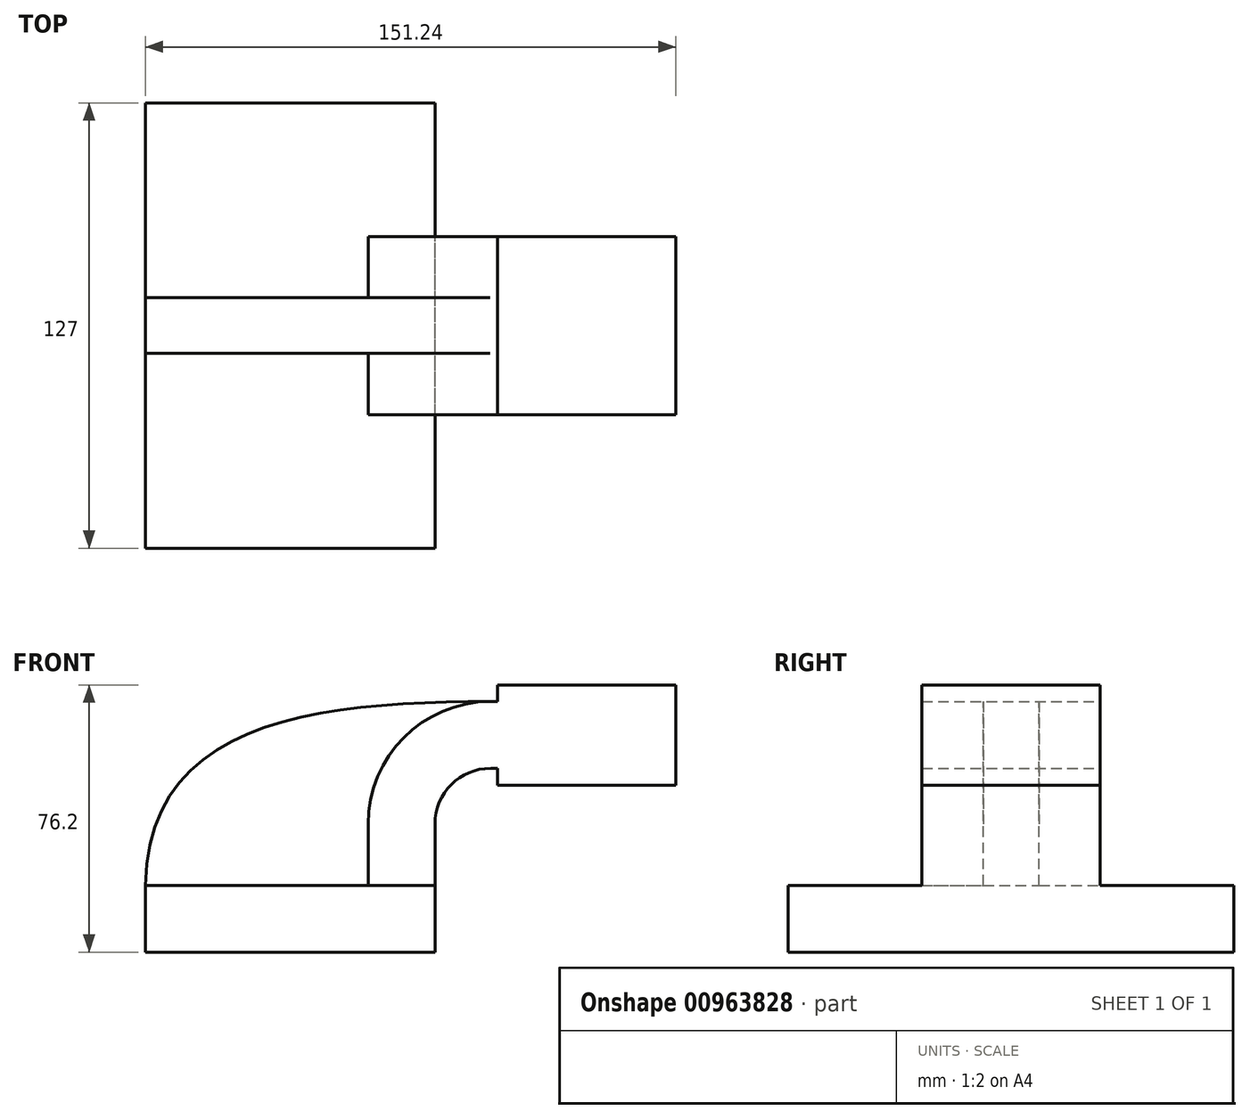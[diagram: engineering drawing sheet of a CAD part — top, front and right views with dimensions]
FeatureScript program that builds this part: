
annotation { "Feature Type Name" : "Feature", "Feature Type Description" : "" }
export const myFeature = defineFeature(function(context is Context, id is Id, definition is map)
    precondition{}
    {
        {
            var Q0;
            Q0=qCreatedBy(makeId("Front.planeOp"),FACE);
            var sketch = newSketch(context, id + "F0", { "sketchPlane" : qUnion([Q0])});
            skLineSegment(sketch, "E0.bottom", {"start": v(-41.28, -9.53) * mm, "end": v(41.28, -9.53) * mm});
            skLineSegment(sketch, "E0.top", {"start": v(-41.28, 9.52) * mm, "end": v(41.28, 9.52) * mm});
            skLineSegment(sketch, "E0.left", {"start": v(-41.28, -9.53) * mm, "end": v(-41.28, 9.53) * mm});
            skLineSegment(sketch, "E0.right", {"start": v(41.28, -9.53) * mm, "end": v(41.28, 9.52) * mm});
            skPoint(sketch, "E0.middle", {"position": v(0, 0) * mm});
            skLineSegment(sketch, "E1.bottom", {"start": v(59.16, 66.67) * mm, "end": v(109.96, 66.67) * mm});
            skLineSegment(sketch, "E1.top", {"start": v(59.16, 38.1) * mm, "end": v(109.96, 38.1) * mm});
            skLineSegment(sketch, "E1.left", {"start": v(59.16, 66.67) * mm, "end": v(59.16, 38.1) * mm});
            skLineSegment(sketch, "E1.right", {"start": v(109.96, 66.67) * mm, "end": v(109.96, 38.1) * mm});
            skPoint(sketch, "E1.middle", {"position": v(84.56, 52.39) * mm});
            skLineSegment(sketch, "E2", {"start": v(41.28, 9.52) * mm, "end": v(41.28, 27) * mm});
            skArc(sketch, "E3", {"start": v(57.15, 42.88) * mm, "mid": v(45.92, 38.23) * mm, "end": v(41.27, 27) * mm});
            skLineSegment(sketch, "E4", {"start": v(57.15, 42.88) * mm, "end": v(59.16, 42.88) * mm});
            skArc(sketch, "E5.0", {"start": v(57.15, 61.93) * mm, "mid": v(32.45, 51.7) * mm, "end": v(22.22, 27) * mm});
            skLineSegment(sketch, "E5.1", {"start": v(22.22, 9.52) * mm, "end": v(22.22, 27) * mm});
            skLineSegment(sketch, "E6", {"start": v(57.15, 61.93) * mm, "end": v(84.56, 61.93) * mm});
            skLineSegment(sketch, "E7", {"start": v(59.16, 42.88) * mm, "end": v(84.56, 42.88) * mm});
            skFitSpline(sketch, "E8", {"points": [v(-41.28, 9.53) * mm, v(57.15, 61.93) * mm], "startDerivative": vector(2.14, 143.61) * mm, "endDerivative": vector(142.97, 0.33) * mm});
            skSolve(sketch);
        }
        {
            var Q0;
            Q0=makeQuery(id+"F0.imprint","IMPRINT",FACE,{"disambiguationData":[TD([[makeQuery(id+"F0.imprint","IMPRINT",EDGE,{"derivedFrom":sQuery(id+"F0.wireOp",EDGE,"E0.bottom")}),1.0]])]});
            extrude(context, id + "F1", {"entities" : qUnion([Q0]), "endBound" : BoundingType.SYMMETRIC, "depth" : 127 * mm, "offsetDistance" : 25.4 * mm});
        }
        {
            var Q0;
            {var subQ0=sQuery(id+"F0.wireOp",EDGE,"E2");Q0=makeQuery(id+"F0.imprint","IMPRINT",FACE,{"disambiguationData":[TD([[makeQuery(id+"F0.imprint","IMPRINT",EDGE,{"derivedFrom":subQ0}),1.0]])]});}
            var Q1;
            {var subQ3=sQuery(id+"F0.wireOp",EDGE,"E1.bottom");Q1=makeQuery(id+"F0.imprint","IMPRINT",FACE,{"disambiguationData":[TD([[makeQuery(id+"F0.imprint","IMPRINT",EDGE,{"derivedFrom":subQ3}),-1.0]])]});}
            extrude(context, id + "F2", {"entities" : qUnion([Q0, Q1]), "operationType" : NewBodyOperationType.ADD, "endBound" : BoundingType.SYMMETRIC, "depth" : 50.8 * mm, "offsetDistance" : 25.4 * mm});
        }
        {
            var Q0;
            {var subQ4=sQuery(id+"F0.wireOp",EDGE,"E5.0");Q0=makeQuery(id+"F0.imprint","IMPRINT",FACE,{"disambiguationData":[TD([[makeQuery(id+"F0.imprint","IMPRINT",EDGE,{"derivedFrom":subQ4}),-1.0]])]});}
            extrude(context, id + "F3", {"entities" : qUnion([Q0]), "operationType" : NewBodyOperationType.ADD, "endBound" : BoundingType.SYMMETRIC, "depth" : 15.88 * mm, "offsetDistance" : 25.4 * mm});
        }
    });
